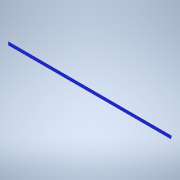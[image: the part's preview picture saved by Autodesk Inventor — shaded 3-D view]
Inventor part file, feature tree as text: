
AUTODESK INVENTOR PART (.ipt)
format: ipt  version: 2020.3 (Build 243373000, 373)  size: 599,040 bytes
history: native  units: mm (DEFAULTED — no unit token found)
features: extrude x2, sketch x2, pattern_linear x1
ambient origin geometry x8: Origin, YZ Plane, XZ Plane, XY Plane, X Axis, Y Axis, Z Axis, Center Point
bodies: Solid1 (feature_tree)
feature tree (5):
  extrude  "Extrusion1"  Depth=5.0mm TaperAngle=0.0deg
  extrude  "Extrusion2"  [1 undecoded]
  pattern_linear  "Rectangular Pattern1"  [2 undecoded]
  sketch  "Sketch_1"  dims[d0=550.0mm d1=0.0mm d2=5.0mm d3=0.0mm]
  sketch  "Sketch_5"  dims[d4=6410.0mm d6=3.14159mm d7=10.0mm d9=0.0mm]
note: 3 required parameter values undecoded (feature->parameter linkage not recoverable at this tier; creation-order binding heuristic only, values carry confidence <= 0.55)
